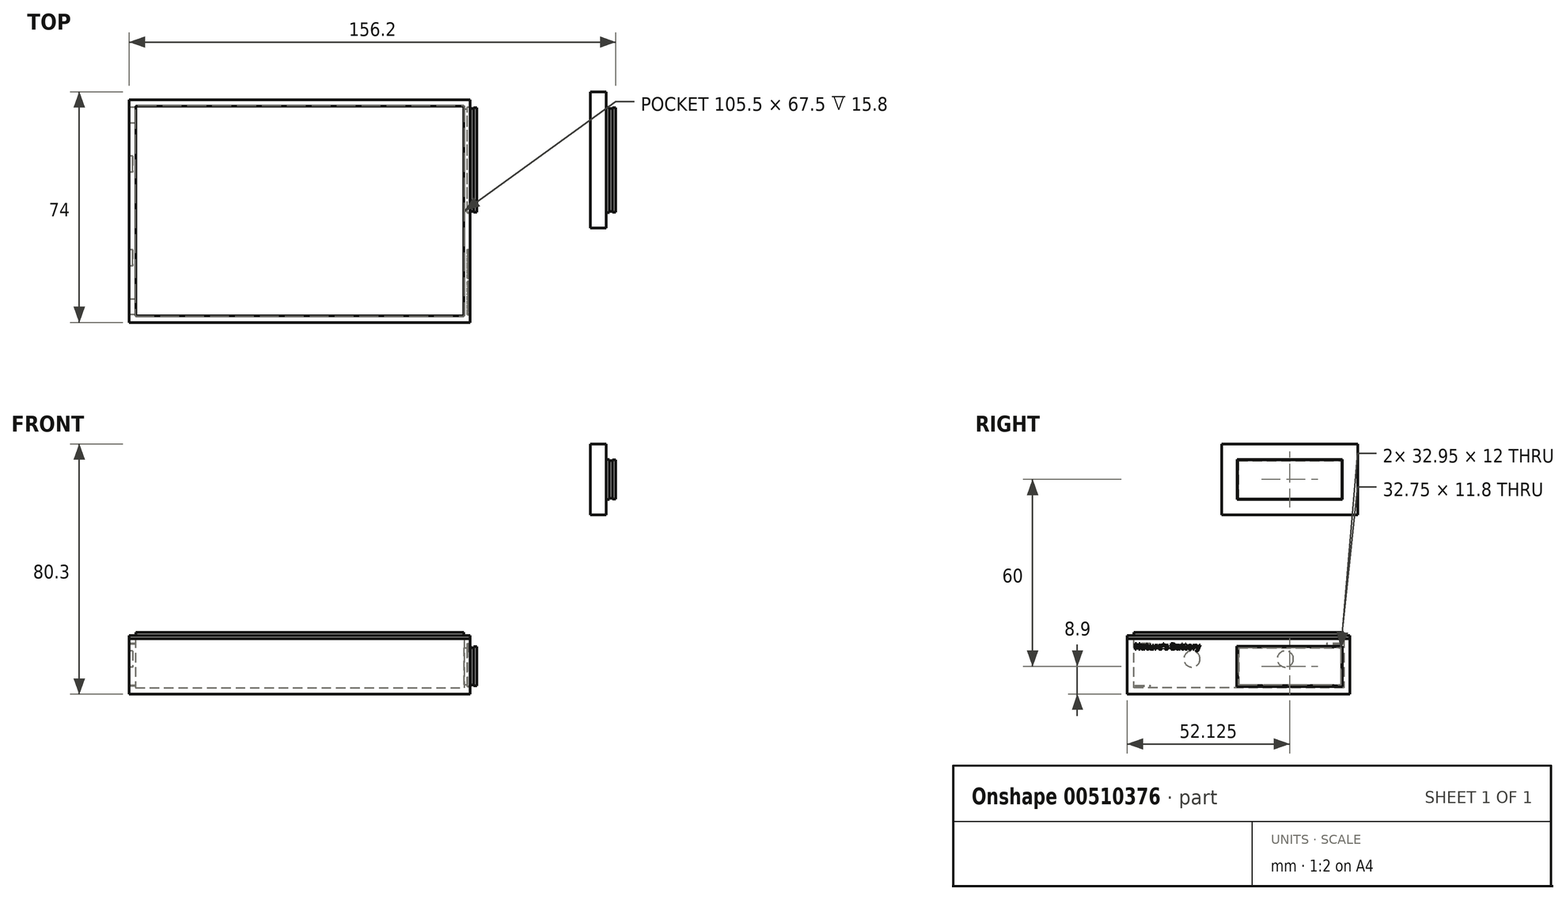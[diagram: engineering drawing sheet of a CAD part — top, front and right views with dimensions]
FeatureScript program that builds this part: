
annotation { "Feature Type Name" : "Feature", "Feature Type Description" : "" }
export const myFeature = defineFeature(function(context is Context, id is Id, definition is map)
    precondition{}
    {
        {
            var Q0;
            Q0=qCreatedBy(makeId("Top.planeOp"),FACE);
            var sketch = newSketch(context, id + "F0", { "sketchPlane" : qUnion([Q0])});
            skLineSegment(sketch, "E0.bottom", {"start": v(-54.75, 35.75) * mm, "end": v(54.75, 35.75) * mm});
            skLineSegment(sketch, "E0.top", {"start": v(-54.75, -35.75) * mm, "end": v(54.75, -35.75) * mm});
            skLineSegment(sketch, "E0.left", {"start": v(-54.75, 35.75) * mm, "end": v(-54.75, -35.75) * mm});
            skLineSegment(sketch, "E0.right", {"start": v(54.75, 35.75) * mm, "end": v(54.75, -35.75) * mm});
            skPoint(sketch, "E0.middle", {"position": v(0, 0) * mm});
            skSolve(sketch);
        }
        {
            var Q0;
            Q0 = qSketchRegion(id + "F0", true);
            extrude(context, id + "F1", {"entities" : qUnion([Q0]), "depth" : 17.8 * mm});
        }
        {
            var Q0;
            Q0=makeQuery(id+"F1.opExtrude","CAP_FACE",FACE,{"disambiguationData":[OSD([sQuery(id+"F0.wireOp",EDGE,"E0.bottom"),sQuery(id+"F0.wireOp",EDGE,"E0.top"),sQuery(id+"F0.wireOp",EDGE,"E0.left"),sQuery(id+"F0.wireOp",EDGE,"E0.right")])],"isStart":false});
            shell(context, id + "F2", {"entities" : qUnion([Q0]), "thickness" : 2 * mm});
        }
        {
            var Q0;
            Q0=makeQuery(id+"F1.opExtrude","CAP_FACE",FACE,{"disambiguationData":[OSD([sQuery(id+"F0.wireOp",EDGE,"E0.bottom"),sQuery(id+"F0.wireOp",EDGE,"E0.top"),sQuery(id+"F0.wireOp",EDGE,"E0.left"),sQuery(id+"F0.wireOp",EDGE,"E0.right")])],"isStart":false});
            var sketch = newSketch(context, id + "F3", { "sketchPlane" : qUnion([Q0])});
            skLineSegment(sketch, "E1.bottom", {"start": v(-54.75, -35.75) * mm, "end": v(54.75, -35.75) * mm});
            skLineSegment(sketch, "E1.top", {"start": v(-54.75, 35.75) * mm, "end": v(54.75, 35.75) * mm});
            skLineSegment(sketch, "E1.left", {"start": v(-54.75, -35.75) * mm, "end": v(-54.75, 35.75) * mm});
            skLineSegment(sketch, "E1.right", {"start": v(54.75, -35.75) * mm, "end": v(54.75, 35.75) * mm});
            skSolve(sketch);
        }
        {
            var Q0;
            Q0 = qSketchRegion(id + "F3", true);
            extrude(context, id + "F4", {"entities" : qUnion([Q0]), "depth" : 1 * mm});
        }
        {
            var Q0;
            Q0=makeQuery(id+"F4.opExtrude","CAP_FACE",FACE,{"disambiguationData":[OSD([sQuery(id+"F3.wireOp",EDGE,"E1.bottom"),sQuery(id+"F3.wireOp",EDGE,"E1.top"),sQuery(id+"F3.wireOp",EDGE,"E1.left"),sQuery(id+"F3.wireOp",EDGE,"E1.right")])],"isStart":false});
            var sketch = newSketch(context, id + "F5", { "sketchPlane" : qUnion([Q0])});
            skPoint(sketch, "E2", {"position": v(52.75, 35.75) * mm});
            skPoint(sketch, "E3", {"position": v(52.65, 33.65) * mm});
            skPoint(sketch, "E4", {"position": v(54.75, 35.75) * mm});
            skPoint(sketch, "E5", {"position": v(54.75, 33.65) * mm});
            skPoint(sketch, "E6", {"position": v(-54.75, -35.75) * mm});
            skPoint(sketch, "E7", {"position": v(-54.75, -33.65) * mm});
            skPoint(sketch, "E8", {"position": v(-52.65, -33.65) * mm});
            skPoint(sketch, "E9", {"position": v(-52.65, -35.75) * mm});
            skLineSegment(sketch, "E10.bottom", {"start": v(-52.65, -33.65) * mm, "end": v(52.65, -33.65) * mm});
            skLineSegment(sketch, "E10.top", {"start": v(-52.65, 33.65) * mm, "end": v(52.65, 33.65) * mm});
            skLineSegment(sketch, "E10.left", {"start": v(-52.65, -33.65) * mm, "end": v(-52.65, 33.65) * mm});
            skLineSegment(sketch, "E10.right", {"start": v(52.65, -33.65) * mm, "end": v(52.65, 33.65) * mm});
            skSolve(sketch);
        }
        {
            var Q0;
            Q0 = qSketchRegion(id + "F5", true);
            extrude(context, id + "F6", {"entities" : qUnion([Q0]), "operationType" : NewBodyOperationType.ADD, "depth" : 1 * mm});
        }
        {
            var Q0;
            Q0=makeQuery(id+"F1.opExtrude","SWEPT_FACE",FACE,{"disambiguationData":[OSD([sQuery(id+"F0.wireOp",EDGE,"E0.left")])]});
            var sketch = newSketch(context, id + "F7", { "sketchPlane" : qUnion([Q0])});
            skPoint(sketch, "E11", {"position": v(33.25, 0) * mm});
            skPoint(sketch, "E12", {"position": v(35.75, 2.5) * mm});
            skPoint(sketch, "E13", {"position": v(35.75, 0) * mm});
            skPoint(sketch, "E14", {"position": v(33.25, 2.5) * mm});
            skLineSegment(sketch, "E15.bottom", {"start": v(33.25, 2.5) * mm, "end": v(28.25, 2.5) * mm});
            skLineSegment(sketch, "E15.top", {"start": v(33.25, 2.8) * mm, "end": v(28.25, 2.8) * mm});
            skLineSegment(sketch, "E15.left", {"start": v(33.25, 2.5) * mm, "end": v(33.25, 2.8) * mm});
            skLineSegment(sketch, "E15.right", {"start": v(28.25, 2.5) * mm, "end": v(28.25, 2.8) * mm});
            skLineSegment(sketch, "E16.bottom", {"start": v(28.25, 16.3) * mm, "end": v(33.25, 16.3) * mm});
            skLineSegment(sketch, "E16.top", {"start": v(28.25, 16) * mm, "end": v(33.25, 16) * mm});
            skLineSegment(sketch, "E16.left", {"start": v(28.25, 16.3) * mm, "end": v(28.25, 16) * mm});
            skLineSegment(sketch, "E16.right", {"start": v(33.25, 16.3) * mm, "end": v(33.25, 16) * mm});
            skPoint(sketch, "E17", {"position": v(-35.75, 0) * mm});
            skPoint(sketch, "E18", {"position": v(-33.25, 0) * mm});
            skPoint(sketch, "E19", {"position": v(-35.75, 2.5) * mm});
            skPoint(sketch, "E20", {"position": v(-33.25, 2.5) * mm});
            skLineSegment(sketch, "E21.bottom", {"start": v(-33.25, 2.5) * mm, "end": v(-28.25, 2.5) * mm});
            skLineSegment(sketch, "E21.top", {"start": v(-33.25, 2.8) * mm, "end": v(-28.25, 2.8) * mm});
            skLineSegment(sketch, "E21.left", {"start": v(-33.25, 2.5) * mm, "end": v(-33.25, 2.8) * mm});
            skLineSegment(sketch, "E21.right", {"start": v(-28.25, 2.5) * mm, "end": v(-28.25, 2.8) * mm});
            skLineSegment(sketch, "E22.bottom", {"start": v(-33.25, 16.3) * mm, "end": v(-28.25, 16.3) * mm});
            skLineSegment(sketch, "E22.top", {"start": v(-33.25, 16) * mm, "end": v(-28.25, 16) * mm});
            skLineSegment(sketch, "E22.left", {"start": v(-33.25, 16.3) * mm, "end": v(-33.25, 16) * mm});
            skLineSegment(sketch, "E22.right", {"start": v(-28.25, 16.3) * mm, "end": v(-28.25, 16) * mm});
            skSolve(sketch);
        }
        {
            var Q0;
            Q0 = qSketchRegion(id + "F7", true);
            extrude(context, id + "F8", {"entities" : qUnion([Q0]), "operationType" : NewBodyOperationType.REMOVE, "oppositeDirection" : true, "depth" : 2 * mm});
        }
        {
            var Q0;
            Q0=makeQuery(id+"F1.opExtrude","SWEPT_FACE",FACE,{"disambiguationData":[OSD([sQuery(id+"F0.wireOp",EDGE,"E0.right")])]});
            var sketch = newSketch(context, id + "F9", { "sketchPlane" : qUnion([Q0])});
            skText(sketch, "E23", { "text": "Nature\'s Battery", "fontName": "OpenSans-Bold.ttf"});
            const initialGuessF9  = {"E23": [-0.0335, 0.01438, 1, 0, 0.00183]};
            skSetInitialGuess(sketch, initialGuessF9);
            skSolve(sketch);
        }
        {
            var Q0;
            Q0 = qSketchRegion(id + "F9", true);
            extrude(context, id + "F10", {"entities" : qUnion([Q0]), "operationType" : NewBodyOperationType.REMOVE, "oppositeDirection" : true, "depth" : 1 * mm});
        }
        {
            var Q0;
            {var subQ0=sQuery(id+"F0.wireOp",EDGE,"E0.bottom");var subQ1=sQuery(id+"F0.wireOp",EDGE,"E0.right");Q0=makeQuery(id+"F10.boolean.opBoolean","SPLIT",FACE,{"disambiguationData":[TD([makeQuery(id+"F1.opExtrude","SWEPT_FACE",FACE,{"disambiguationData":[OSD([subQ0])]})])],"derivedFrom":makeQuery(id+"F1.opExtrude","SWEPT_FACE",FACE,{"disambiguationData":[OSD([subQ1])]})});}
            var sketch = newSketch(context, id + "F11", { "sketchPlane" : qUnion([Q0])});
            skPoint(sketch, "E24", {"position": v(35.75, 0) * mm});
            skPoint(sketch, "E25", {"position": v(32.75, 0) * mm});
            skPoint(sketch, "E26", {"position": v(32.75, 3) * mm});
            skPoint(sketch, "E27", {"position": v(35.75, 3) * mm});
            skPoint(sketch, "E28", {"position": v(32.75, 14.8) * mm});
            skPoint(sketch, "E29", {"position": v(32.75, 17.8) * mm});
            skPoint(sketch, "E30", {"position": v(35.75, 17.8) * mm});
            skPoint(sketch, "E31", {"position": v(35.75, 14.8) * mm});
            skLineSegment(sketch, "E32.bottom", {"start": v(32.75, 3) * mm, "end": v(0, 3) * mm});
            skLineSegment(sketch, "E32.top", {"start": v(32.75, 14.8) * mm, "end": v(0, 14.8) * mm});
            skLineSegment(sketch, "E32.left", {"start": v(32.75, 3) * mm, "end": v(32.75, 14.8) * mm});
            skLineSegment(sketch, "E32.right", {"start": v(0, 3) * mm, "end": v(0, 14.8) * mm});
            skSolve(sketch);
        }
        {
            var Q0;
            Q0 = qSketchRegion(id + "F11", true);
            extrude(context, id + "F12", {"entities" : qUnion([Q0]), "operationType" : NewBodyOperationType.REMOVE, "oppositeDirection" : true, "depth" : 2 * mm});
        }
        {
            var Q0;
            {var subQ0=sQuery(id+"F0.wireOp",EDGE,"E0.bottom");var subQ1=sQuery(id+"F0.wireOp",EDGE,"E0.right");Q0=makeQuery(id+"F10.boolean.opBoolean","SPLIT",FACE,{"disambiguationData":[TD([makeQuery(id+"F1.opExtrude","SWEPT_FACE",FACE,{"disambiguationData":[OSD([subQ0])]})])],"derivedFrom":makeQuery(id+"F1.opExtrude","SWEPT_FACE",FACE,{"disambiguationData":[OSD([subQ1])]})});}
            var sketch = newSketch(context, id + "F13", { "sketchPlane" : qUnion([Q0])});
            skPoint(sketch, "E33", {"position": v(33.35, 15.4) * mm});
            skPoint(sketch, "E34", {"position": v(32.75, 14.8) * mm});
            skPoint(sketch, "E35", {"position": v(32.75, 15.4) * mm});
            skPoint(sketch, "E36", {"position": v(33.35, 14.8) * mm});
            skPoint(sketch, "E37", {"position": v(0, 3) * mm});
            skPoint(sketch, "E38", {"position": v(-0.6, 3) * mm});
            skPoint(sketch, "E39", {"position": v(0, 2.4) * mm});
            skPoint(sketch, "E40", {"position": v(-0.6, 2.4) * mm});
            skLineSegment(sketch, "E41.bottom", {"start": v(-0.6, 2.4) * mm, "end": v(33.35, 2.4) * mm});
            skLineSegment(sketch, "E41.top", {"start": v(-0.6, 15.4) * mm, "end": v(33.35, 15.4) * mm});
            skLineSegment(sketch, "E41.left", {"start": v(-0.6, 2.4) * mm, "end": v(-0.6, 15.4) * mm});
            skLineSegment(sketch, "E41.right", {"start": v(33.35, 2.4) * mm, "end": v(33.35, 15.4) * mm});
            skSolve(sketch);
        }
        {
            var Q0;
            Q0 = qSketchRegion(id + "F13", true);
            extrude(context, id + "F14", {"entities" : qUnion([Q0]), "operationType" : NewBodyOperationType.REMOVE, "oppositeDirection" : true, "depth" : 1 * mm});
        }
        {
            var Q0;
            Q0=makeQuery(id+"F14.boolean.opBoolean","COPY",FACE,{"derivedFrom":makeQuery(id+"F14.opExtrude","CAP_FACE",FACE,{"disambiguationData":[OSD([sQuery(id+"F13.wireOp",EDGE,"E41.bottom"),sQuery(id+"F13.wireOp",EDGE,"E41.top"),sQuery(id+"F13.wireOp",EDGE,"E41.left"),sQuery(id+"F13.wireOp",EDGE,"E41.right")])],"isStart":false})});
            var sketch = newSketch(context, id + "F15", { "sketchPlane" : qUnion([Q0])});
            skPoint(sketch, "E42", {"position": v(33.35, 15.4) * mm});
            skPoint(sketch, "E43", {"position": v(33.35, 15.3) * mm});
            skPoint(sketch, "E44", {"position": v(33.25, 15.4) * mm});
            skPoint(sketch, "E45", {"position": v(33.25, 15.3) * mm});
            skPoint(sketch, "E46", {"position": v(-0.6, 2.4) * mm});
            skPoint(sketch, "E47", {"position": v(-0.5, 2.4) * mm});
            skPoint(sketch, "E48", {"position": v(-0.6, 2.5) * mm});
            skPoint(sketch, "E49", {"position": v(-0.5, 2.5) * mm});
            skLineSegment(sketch, "E50.bottom", {"start": v(-0.5, 2.5) * mm, "end": v(33.25, 2.5) * mm});
            skLineSegment(sketch, "E50.top", {"start": v(-0.5, 15.3) * mm, "end": v(33.25, 15.3) * mm});
            skLineSegment(sketch, "E50.left", {"start": v(-0.5, 2.5) * mm, "end": v(-0.5, 15.3) * mm});
            skLineSegment(sketch, "E50.right", {"start": v(33.25, 2.5) * mm, "end": v(33.25, 15.3) * mm});
            skSolve(sketch);
        }
        {
            var Q0;
            Q0 = qSketchRegion(id + "F15", true);
            extrude(context, id + "F16", {"entities" : qUnion([Q0]), "depth" : 1.1 * mm});
        }
        {
            var Q0;
            Q0=makeQuery(id+"F16.opExtrude","CAP_FACE",FACE,{"disambiguationData":[OSD([sQuery(id+"F15.wireOp",EDGE,"E50.bottom"),sQuery(id+"F15.wireOp",EDGE,"E50.top"),sQuery(id+"F15.wireOp",EDGE,"E50.left"),sQuery(id+"F15.wireOp",EDGE,"E50.right")])],"isStart":false});
            var sketch = newSketch(context, id + "F17", { "sketchPlane" : qUnion([Q0])});
            skPoint(sketch, "E51", {"position": v(-0.5, 15.3) * mm});
            skPoint(sketch, "E52", {"position": v(-0.1, 15.3) * mm});
            skPoint(sketch, "E53", {"position": v(-0.5, 14.9) * mm});
            skPoint(sketch, "E54", {"position": v(-0.1, 14.9) * mm});
            skPoint(sketch, "E55", {"position": v(33.25, 2.5) * mm});
            skPoint(sketch, "E56", {"position": v(32.85, 2.5) * mm});
            skPoint(sketch, "E57", {"position": v(33.25, 2.9) * mm});
            skPoint(sketch, "E58", {"position": v(32.85, 2.9) * mm});
            skLineSegment(sketch, "E59.bottom", {"start": v(-0.1, 14.9) * mm, "end": v(32.85, 14.9) * mm});
            skLineSegment(sketch, "E59.top", {"start": v(-0.1, 2.9) * mm, "end": v(32.85, 2.9) * mm});
            skLineSegment(sketch, "E59.left", {"start": v(-0.1, 14.9) * mm, "end": v(-0.1, 2.9) * mm});
            skLineSegment(sketch, "E59.right", {"start": v(32.85, 14.9) * mm, "end": v(32.85, 2.9) * mm});
            skSolve(sketch);
        }
        {
            var Q0;
            Q0 = qSketchRegion(id + "F17", true);
            extrude(context, id + "F18", {"entities" : qUnion([Q0]), "operationType" : NewBodyOperationType.ADD, "depth" : 2 * mm});
        }
        {
            var Q0;
            Q0=makeQuery(id+"F18.opExtrude","SWEPT_FACE",FACE,{"disambiguationData":[OSD([sQuery(id+"F17.wireOp",EDGE,"E59.left")])]});
            var sketch = newSketch(context, id + "F19", { "sketchPlane" : qUnion([Q0])});
            skLineSegment(sketch, "E60.bottom", {"start": v(56.85, 14.9) * mm, "end": v(55.85, 14.9) * mm});
            skLineSegment(sketch, "E60.top", {"start": v(56.85, 2.9) * mm, "end": v(55.85, 2.9) * mm});
            skLineSegment(sketch, "E60.left", {"start": v(56.85, 14.9) * mm, "end": v(56.85, 2.9) * mm});
            skLineSegment(sketch, "E60.right", {"start": v(55.85, 14.9) * mm, "end": v(55.85, 2.9) * mm});
            skSolve(sketch);
        }
        {
            var Q0;
            Q0 = qSketchRegion(id + "F19", true);
            extrude(context, id + "F20", {"entities" : qUnion([Q0]), "operationType" : NewBodyOperationType.ADD, "depth" : .3 * mm});
        }
        {
            var Q0;
            Q0=makeQuery(id+"F18.opExtrude","SWEPT_FACE",FACE,{"disambiguationData":[OSD([sQuery(id+"F17.wireOp",EDGE,"E59.right")])]});
            var sketch = newSketch(context, id + "F21", { "sketchPlane" : qUnion([Q0])});
            skLineSegment(sketch, "E61.bottom", {"start": v(-56.85, 14.9) * mm, "end": v(-55.85, 14.9) * mm});
            skLineSegment(sketch, "E61.top", {"start": v(-56.85, 2.9) * mm, "end": v(-55.85, 2.9) * mm});
            skLineSegment(sketch, "E61.left", {"start": v(-56.85, 14.9) * mm, "end": v(-56.85, 2.9) * mm});
            skLineSegment(sketch, "E61.right", {"start": v(-55.85, 14.9) * mm, "end": v(-55.85, 2.9) * mm});
            skSolve(sketch);
        }
        {
            var Q0;
            Q0 = qSketchRegion(id + "F21", true);
            extrude(context, id + "F22", {"entities" : qUnion([Q0]), "operationType" : NewBodyOperationType.ADD, "depth" : .3 * mm});
        }
        {
            var Q0;
            Q0=makeQuery(id+"F22.boolean.opBoolean","MERGE",FACE,{"derivedFrom":[makeQuery(id+"F20.boolean.opBoolean","MERGE",FACE,{"derivedFrom":[makeQuery(id+"F18.opExtrude","SWEPT_FACE",FACE,{"disambiguationData":[OSD([sQuery(id+"F17.wireOp",EDGE,"E59.bottom")])]}),makeQuery(id+"F20.opExtrude","SWEPT_FACE",FACE,{"disambiguationData":[OSD([sQuery(id+"F19.wireOp",EDGE,"E60.bottom")])]})]}),makeQuery(id+"F22.opExtrude","SWEPT_FACE",FACE,{"disambiguationData":[OSD([sQuery(id+"F21.wireOp",EDGE,"E61.bottom")])]})]});
            var sketch = newSketch(context, id + "F23", { "sketchPlane" : qUnion([Q0])});
            skLineSegment(sketch, "E62.bottom", {"start": v(55.85, -0.4) * mm, "end": v(56.85, -0.4) * mm});
            skLineSegment(sketch, "E62.top", {"start": v(55.85, 33.15) * mm, "end": v(56.85, 33.15) * mm});
            skLineSegment(sketch, "E62.left", {"start": v(55.85, -0.4) * mm, "end": v(55.85, 33.15) * mm});
            skLineSegment(sketch, "E62.right", {"start": v(56.85, -0.4) * mm, "end": v(56.85, 33.15) * mm});
            skSolve(sketch);
        }
        {
            var Q0;
            Q0 = qSketchRegion(id + "F23", true);
            extrude(context, id + "F24", {"entities" : qUnion([Q0]), "operationType" : NewBodyOperationType.ADD, "depth" : .3 * mm});
        }
        {
            var Q0;
            Q0=makeQuery(id+"F22.boolean.opBoolean","MERGE",FACE,{"derivedFrom":[makeQuery(id+"F20.boolean.opBoolean","MERGE",FACE,{"derivedFrom":[makeQuery(id+"F18.opExtrude","SWEPT_FACE",FACE,{"disambiguationData":[OSD([sQuery(id+"F17.wireOp",EDGE,"E59.top")])]}),makeQuery(id+"F20.opExtrude","SWEPT_FACE",FACE,{"disambiguationData":[OSD([sQuery(id+"F19.wireOp",EDGE,"E60.top")])]})]}),makeQuery(id+"F22.opExtrude","SWEPT_FACE",FACE,{"disambiguationData":[OSD([sQuery(id+"F21.wireOp",EDGE,"E61.top")])]})]});
            var sketch = newSketch(context, id + "F25", { "sketchPlane" : qUnion([Q0])});
            skLineSegment(sketch, "E63.bottom", {"start": v(55.85, 0.4) * mm, "end": v(56.85, 0.4) * mm});
            skLineSegment(sketch, "E63.top", {"start": v(55.85, -33.15) * mm, "end": v(56.85, -33.15) * mm});
            skLineSegment(sketch, "E63.left", {"start": v(55.85, 0.4) * mm, "end": v(55.85, -33.15) * mm});
            skLineSegment(sketch, "E63.right", {"start": v(56.85, 0.4) * mm, "end": v(56.85, -33.15) * mm});
            skSolve(sketch);
        }
        {
            var Q0;
            Q0 = qSketchRegion(id + "F25", true);
            extrude(context, id + "F26", {"entities" : qUnion([Q0]), "operationType" : NewBodyOperationType.ADD, "depth" : .3 * mm});
        }
        {
            var Q0;
            Q0=makeQuery(id+"F1.opExtrude","SWEPT_FACE",FACE,{"disambiguationData":[OSD([sQuery(id+"F0.wireOp",EDGE,"E0.left")])]});
            var sketch = newSketch(context, id + "F27", { "sketchPlane" : qUnion([Q0])});
            skPoint(sketch, "E64", {"position": v(0, 11.24) * mm});
            skPoint(sketch, "E64.positionSnap0", {"position": v(0, 17.8) * mm});
            skCircle(sketch, "E65", {"center": v(-15, 11.24) * mm, "radius": 2.6 * mm});
            skCircle(sketch, "E66", {"center": v(15, 11.25) * mm, "radius": 2.6 * mm});
            skSolve(sketch);
        }
        {
            var Q0;
            Q0 = qSketchRegion(id + "F27", true);
            extrude(context, id + "F28", {"entities" : qUnion([Q0]), "operationType" : NewBodyOperationType.REMOVE, "oppositeDirection" : true, "depth" : 1.1 * mm});
        }
        {
            var Q0;
            Q0=makeQuery(id+"F16.opExtrude","SWEPT_BODY",BODY,{"disambiguationData":[OSD([sQuery(id+"F15.wireOp",EDGE,"E50.bottom"),sQuery(id+"F15.wireOp",EDGE,"E50.top"),sQuery(id+"F15.wireOp",EDGE,"E50.left"),sQuery(id+"F15.wireOp",EDGE,"E50.right")])]});
            transform(context, id + "F29", {"entities" : qUnion([Q0]), "transformType" : TransformType.TRANSLATION_3D, "dx" : 0 * mm, "dy" : 0 * mm, "dz" : 0 * mm, "makeCopy" : true});
        }
        {
            var Q0;
            Q0=makeQuery(id+"F29.opPattern","COPY",BODY,{"derivedFrom":makeQuery(id+"F16.opExtrude","SWEPT_BODY",BODY,{"disambiguationData":[OSD([sQuery(id+"F15.wireOp",EDGE,"E50.bottom"),sQuery(id+"F15.wireOp",EDGE,"E50.top"),sQuery(id+"F15.wireOp",EDGE,"E50.left"),sQuery(id+"F15.wireOp",EDGE,"E50.right")])]}),"instanceName":"1"});
            deleteBodies(context, id + "F30", {"entities" : qUnion([Q0])});
        }
        {
            var Q0;
            Q0=makeQuery(id+"F16.opExtrude","SWEPT_BODY",BODY,{"disambiguationData":[OSD([sQuery(id+"F15.wireOp",EDGE,"E50.bottom"),sQuery(id+"F15.wireOp",EDGE,"E50.top"),sQuery(id+"F15.wireOp",EDGE,"E50.left"),sQuery(id+"F15.wireOp",EDGE,"E50.right")])]});
            transform(context, id + "F31", {"entities" : qUnion([Q0]), "transformType" : TransformType.TRANSLATION_3D, "dx" : 76 * mm, "dy" : 0 * mm, "dz" : 0 * mm, "makeCopy" : true});
        }
        {
            var Q0;
            Q0=makeQuery(id+"F31.opPattern","COPY",FACE,{"derivedFrom":makeQuery(id+"F24.opExtrude","CAP_FACE",FACE,{"disambiguationData":[OSD([sQuery(id+"F23.wireOp",EDGE,"E62.bottom"),sQuery(id+"F23.wireOp",EDGE,"E62.top"),sQuery(id+"F23.wireOp",EDGE,"E62.left"),sQuery(id+"F23.wireOp",EDGE,"E62.right")])],"isStart":false}),"instanceName":"1"});
            var sketch = newSketch(context, id + "F32", { "sketchPlane" : qUnion([Q0])});
            skLineSegment(sketch, "E67.bottom", {"start": v(131.85, 33.15) * mm, "end": v(132.85, 33.15) * mm});
            skLineSegment(sketch, "E67.top", {"start": v(131.85, -0.4) * mm, "end": v(132.85, -0.4) * mm});
            skLineSegment(sketch, "E67.left", {"start": v(131.85, 33.15) * mm, "end": v(131.85, -0.4) * mm});
            skLineSegment(sketch, "E67.right", {"start": v(132.85, 33.15) * mm, "end": v(132.85, -0.4) * mm});
            skSolve(sketch);
        }
        {
            var Q0;
            Q0 = qSketchRegion(id + "F32", true);
            extrude(context, id + "F33", {"entities" : qUnion([Q0]), "depth" : 5 * mm, "offsetDistance" : 25 * mm});
        }
        {
            var Q0;
            Q0=makeQuery(id+"F31.opPattern","COPY",FACE,{"derivedFrom":makeQuery(id+"F22.boolean.opBoolean","MERGE",FACE,{"derivedFrom":[makeQuery(id+"F20.boolean.opBoolean","MERGE",FACE,{"derivedFrom":[makeQuery(id+"F18.opExtrude","SWEPT_FACE",FACE,{"disambiguationData":[OSD([sQuery(id+"F17.wireOp",EDGE,"E59.bottom")])]}),makeQuery(id+"F20.opExtrude","SWEPT_FACE",FACE,{"disambiguationData":[OSD([sQuery(id+"F19.wireOp",EDGE,"E60.bottom")])]})]}),makeQuery(id+"F22.opExtrude","SWEPT_FACE",FACE,{"disambiguationData":[OSD([sQuery(id+"F21.wireOp",EDGE,"E61.bottom")])]})]}),"instanceName":"1"});
            var sketch = newSketch(context, id + "F34", { "sketchPlane" : qUnion([Q0])});
            skLineSegment(sketch, "E68.bottom", {"start": v(131.85, 32.85) * mm, "end": v(130.85, 32.85) * mm});
            skLineSegment(sketch, "E68.top", {"start": v(131.85, -0.1) * mm, "end": v(130.85, -0.1) * mm});
            skLineSegment(sketch, "E68.left", {"start": v(131.85, 32.85) * mm, "end": v(131.85, -0.1) * mm});
            skLineSegment(sketch, "E68.right", {"start": v(130.85, 32.85) * mm, "end": v(130.85, -0.1) * mm});
            skSolve(sketch);
        }
        {
            var Q0;
            Q0 = qSketchRegion(id + "F34", true);
            extrude(context, id + "F35", {"entities" : qUnion([Q0]), "depth" : 5.3 * mm, "offsetDistance" : 25 * mm});
        }
        {
            var Q0;
            Q0=makeQuery(id+"F31.opPattern","COPY",FACE,{"derivedFrom":makeQuery(id+"F16.opExtrude","SWEPT_FACE",FACE,{"disambiguationData":[OSD([sQuery(id+"F15.wireOp",EDGE,"E50.top")])]}),"instanceName":"1"});
            var sketch = newSketch(context, id + "F36", { "sketchPlane" : qUnion([Q0])});
            skLineSegment(sketch, "E69.bottom", {"start": v(130.85, 33.25) * mm, "end": v(129.75, 33.25) * mm});
            skLineSegment(sketch, "E69.top", {"start": v(130.85, -0.5) * mm, "end": v(129.75, -0.5) * mm});
            skLineSegment(sketch, "E69.left", {"start": v(130.85, 33.25) * mm, "end": v(130.85, -0.5) * mm});
            skLineSegment(sketch, "E69.right", {"start": v(129.75, 33.25) * mm, "end": v(129.75, -0.5) * mm});
            skSolve(sketch);
        }
        {
            var Q0;
            Q0 = qSketchRegion(id + "F36", true);
            extrude(context, id + "F37", {"entities" : qUnion([Q0]), "depth" : 4.9 * mm, "offsetDistance" : 25 * mm});
        }
        {
            var Q0;
            Q0=makeQuery(id+"F31.opPattern","COPY",FACE,{"derivedFrom":makeQuery(id+"F22.boolean.opBoolean","MERGE",FACE,{"derivedFrom":[makeQuery(id+"F20.boolean.opBoolean","MERGE",FACE,{"derivedFrom":[makeQuery(id+"F18.opExtrude","SWEPT_FACE",FACE,{"disambiguationData":[OSD([sQuery(id+"F17.wireOp",EDGE,"E59.top")])]}),makeQuery(id+"F20.opExtrude","SWEPT_FACE",FACE,{"disambiguationData":[OSD([sQuery(id+"F19.wireOp",EDGE,"E60.top")])]})]}),makeQuery(id+"F22.opExtrude","SWEPT_FACE",FACE,{"disambiguationData":[OSD([sQuery(id+"F21.wireOp",EDGE,"E61.top")])]})]}),"instanceName":"1"});
            var sketch = newSketch(context, id + "F38", { "sketchPlane" : qUnion([Q0])});
            skLineSegment(sketch, "E70.bottom", {"start": v(130.85, 0.1) * mm, "end": v(131.85, 0.1) * mm});
            skLineSegment(sketch, "E70.top", {"start": v(130.85, -32.85) * mm, "end": v(131.85, -32.85) * mm});
            skLineSegment(sketch, "E70.left", {"start": v(130.85, 0.1) * mm, "end": v(130.85, -32.85) * mm});
            skLineSegment(sketch, "E70.right", {"start": v(131.85, 0.1) * mm, "end": v(131.85, -32.85) * mm});
            skSolve(sketch);
        }
        {
            var Q0;
            Q0 = qSketchRegion(id + "F38", true);
            extrude(context, id + "F39", {"entities" : qUnion([Q0]), "depth" : 5.4 * mm, "offsetDistance" : 25 * mm});
        }
        {
            var Q0;
            Q0=makeQuery(id+"F31.opPattern","COPY",FACE,{"derivedFrom":makeQuery(id+"F26.opExtrude","CAP_FACE",FACE,{"disambiguationData":[OSD([sQuery(id+"F25.wireOp",EDGE,"E63.bottom"),sQuery(id+"F25.wireOp",EDGE,"E63.top"),sQuery(id+"F25.wireOp",EDGE,"E63.left"),sQuery(id+"F25.wireOp",EDGE,"E63.right")])],"isStart":false}),"instanceName":"1"});
            var sketch = newSketch(context, id + "F40", { "sketchPlane" : qUnion([Q0])});
            skLineSegment(sketch, "E71.bottom", {"start": v(131.85, -33.15) * mm, "end": v(132.85, -33.15) * mm});
            skLineSegment(sketch, "E71.top", {"start": v(131.85, 0.4) * mm, "end": v(132.85, 0.4) * mm});
            skLineSegment(sketch, "E71.left", {"start": v(131.85, -33.15) * mm, "end": v(131.85, 0.4) * mm});
            skLineSegment(sketch, "E71.right", {"start": v(132.85, -33.15) * mm, "end": v(132.85, 0.4) * mm});
            skSolve(sketch);
        }
        {
            var Q0;
            Q0 = qSketchRegion(id + "F40", true);
            extrude(context, id + "F41", {"entities" : qUnion([Q0]), "depth" : 5.1 * mm, "offsetDistance" : 25 * mm});
        }
        {
            var Q0;
            Q0=makeQuery(id+"F31.opPattern","COPY",FACE,{"derivedFrom":makeQuery(id+"F16.opExtrude","SWEPT_FACE",FACE,{"disambiguationData":[OSD([sQuery(id+"F15.wireOp",EDGE,"E50.bottom")])]}),"instanceName":"1"});
            var sketch = newSketch(context, id + "F42", { "sketchPlane" : qUnion([Q0])});
            skLineSegment(sketch, "E72.bottom", {"start": v(130.85, 0.5) * mm, "end": v(129.75, 0.5) * mm});
            skLineSegment(sketch, "E72.top", {"start": v(130.85, -33.25) * mm, "end": v(129.75, -33.25) * mm});
            skLineSegment(sketch, "E72.left", {"start": v(130.85, 0.5) * mm, "end": v(130.85, -33.25) * mm});
            skLineSegment(sketch, "E72.right", {"start": v(129.75, 0.5) * mm, "end": v(129.75, -33.25) * mm});
            skSolve(sketch);
        }
        {
            var Q0;
            Q0 = qSketchRegion(id + "F42", true);
            extrude(context, id + "F43", {"entities" : qUnion([Q0]), "depth" : 5 * mm, "offsetDistance" : 25 * mm});
        }
        {
            var Q0;
            Q0=makeQuery(id+"F39.opExtrude","SWEPT_FACE",FACE,{"disambiguationData":[OSD([sQuery(id+"F38.wireOp",EDGE,"E70.bottom")])]});
            var sketch = newSketch(context, id + "F44", { "sketchPlane" : qUnion([Q0])});
            skLineSegment(sketch, "E73.bottom", {"start": v(131.85, -2.5) * mm, "end": v(130.85, -2.5) * mm});
            skLineSegment(sketch, "E73.top", {"start": v(131.85, 2.9) * mm, "end": v(130.85, 2.9) * mm});
            skLineSegment(sketch, "E73.left", {"start": v(131.85, -2.5) * mm, "end": v(131.85, 2.9) * mm});
            skLineSegment(sketch, "E73.right", {"start": v(130.85, -2.5) * mm, "end": v(130.85, 2.9) * mm});
            skSolve(sketch);
        }
        {
            var Q0;
            Q0 = qSketchRegion(id + "F44", true);
            extrude(context, id + "F45", {"entities" : qUnion([Q0]), "depth" : 5.1 * mm, "offsetDistance" : 25 * mm});
        }
        {
            var Q0;
            Q0=makeQuery(id+"F43.opExtrude","SWEPT_FACE",FACE,{"disambiguationData":[OSD([sQuery(id+"F42.wireOp",EDGE,"E72.bottom")])]});
            var sketch = newSketch(context, id + "F46", { "sketchPlane" : qUnion([Q0])});
            skLineSegment(sketch, "E74.bottom", {"start": v(130.85, -2.5) * mm, "end": v(129.75, -2.5) * mm});
            skLineSegment(sketch, "E74.top", {"start": v(130.85, 2.5) * mm, "end": v(129.75, 2.5) * mm});
            skLineSegment(sketch, "E74.left", {"start": v(130.85, -2.5) * mm, "end": v(130.85, 2.5) * mm});
            skLineSegment(sketch, "E74.right", {"start": v(129.75, -2.5) * mm, "end": v(129.75, 2.5) * mm});
            skSolve(sketch);
        }
        {
            var Q0;
            Q0 = qSketchRegion(id + "F46", true);
            extrude(context, id + "F47", {"entities" : qUnion([Q0]), "depth" : 4.9 * mm, "offsetDistance" : 25 * mm});
        }
        {
            var Q0;
            Q0=makeQuery(id+"F41.opExtrude","SWEPT_FACE",FACE,{"disambiguationData":[OSD([sQuery(id+"F40.wireOp",EDGE,"E71.top")])]});
            var sketch = newSketch(context, id + "F48", { "sketchPlane" : qUnion([Q0])});
            skLineSegment(sketch, "E75.bottom", {"start": v(132.85, -2.5) * mm, "end": v(131.85, -2.5) * mm});
            skLineSegment(sketch, "E75.top", {"start": v(132.85, 2.6) * mm, "end": v(131.85, 2.6) * mm});
            skLineSegment(sketch, "E75.left", {"start": v(132.85, -2.5) * mm, "end": v(132.85, 2.6) * mm});
            skLineSegment(sketch, "E75.right", {"start": v(131.85, -2.5) * mm, "end": v(131.85, 2.6) * mm});
            skSolve(sketch);
        }
        {
            var Q0;
            Q0 = qSketchRegion(id + "F48", true);
            extrude(context, id + "F49", {"entities" : qUnion([Q0]), "depth" : 4.9 * mm, "offsetDistance" : 25 * mm});
        }
        {
            var Q0;
            Q0=makeQuery(id+"F31.opPattern","COPY",FACE,{"derivedFrom":makeQuery(id+"F26.boolean.opBoolean","MERGE",FACE,{"derivedFrom":[makeQuery(id+"F24.boolean.opBoolean","MERGE",FACE,{"derivedFrom":[makeQuery(id+"F20.opExtrude","CAP_FACE",FACE,{"disambiguationData":[OSD([sQuery(id+"F19.wireOp",EDGE,"E60.bottom"),sQuery(id+"F19.wireOp",EDGE,"E60.top"),sQuery(id+"F19.wireOp",EDGE,"E60.left"),sQuery(id+"F19.wireOp",EDGE,"E60.right")])],"isStart":false}),makeQuery(id+"F24.opExtrude","SWEPT_FACE",FACE,{"disambiguationData":[OSD([sQuery(id+"F23.wireOp",EDGE,"E62.bottom")])]})]}),makeQuery(id+"F26.opExtrude","SWEPT_FACE",FACE,{"disambiguationData":[OSD([sQuery(id+"F25.wireOp",EDGE,"E63.bottom")])]})]}),"instanceName":"1"});
            var sketch = newSketch(context, id + "F50", { "sketchPlane" : qUnion([Q0])});
            skLineSegment(sketch, "E76.bottom", {"start": v(132.85, 2.6) * mm, "end": v(131.85, 2.6) * mm});
            skLineSegment(sketch, "E76.top", {"start": v(132.85, 15.2) * mm, "end": v(131.85, 15.2) * mm});
            skLineSegment(sketch, "E76.left", {"start": v(132.85, 2.6) * mm, "end": v(132.85, 15.2) * mm});
            skLineSegment(sketch, "E76.right", {"start": v(131.85, 2.6) * mm, "end": v(131.85, 15.2) * mm});
            skSolve(sketch);
        }
        {
            var Q0;
            Q0 = qSketchRegion(id + "F50", true);
            extrude(context, id + "F51", {"entities" : qUnion([Q0]), "depth" : 4.9 * mm, "offsetDistance" : 25 * mm});
        }
        {
            var Q0;
            Q0=makeQuery(id+"F31.opPattern","COPY",FACE,{"derivedFrom":makeQuery(id+"F18.opExtrude","SWEPT_FACE",FACE,{"disambiguationData":[OSD([sQuery(id+"F17.wireOp",EDGE,"E59.left")])]}),"instanceName":"1"});
            var sketch = newSketch(context, id + "F52", { "sketchPlane" : qUnion([Q0])});
            skLineSegment(sketch, "E77.bottom", {"start": v(131.85, 2.9) * mm, "end": v(130.85, 2.9) * mm});
            skLineSegment(sketch, "E77.top", {"start": v(131.85, 14.9) * mm, "end": v(130.85, 14.9) * mm});
            skLineSegment(sketch, "E77.left", {"start": v(131.85, 2.9) * mm, "end": v(131.85, 14.9) * mm});
            skLineSegment(sketch, "E77.right", {"start": v(130.85, 2.9) * mm, "end": v(130.85, 14.9) * mm});
            skSolve(sketch);
        }
        {
            var Q0;
            Q0 = qSketchRegion(id + "F52", true);
            extrude(context, id + "F53", {"entities" : qUnion([Q0]), "depth" : 5 * mm, "offsetDistance" : 25 * mm});
        }
        {
            var Q0;
            Q0=makeQuery(id+"F31.opPattern","COPY",FACE,{"derivedFrom":makeQuery(id+"F16.opExtrude","SWEPT_FACE",FACE,{"disambiguationData":[OSD([sQuery(id+"F15.wireOp",EDGE,"E50.left")])]}),"instanceName":"1"});
            var sketch = newSketch(context, id + "F54", { "sketchPlane" : qUnion([Q0])});
            skLineSegment(sketch, "E78.bottom", {"start": v(130.85, 2.5) * mm, "end": v(129.75, 2.5) * mm});
            skLineSegment(sketch, "E78.top", {"start": v(130.85, 15.3) * mm, "end": v(129.75, 15.3) * mm});
            skLineSegment(sketch, "E78.left", {"start": v(130.85, 2.5) * mm, "end": v(130.85, 15.3) * mm});
            skLineSegment(sketch, "E78.right", {"start": v(129.75, 2.5) * mm, "end": v(129.75, 15.3) * mm});
            skSolve(sketch);
        }
        {
            var Q0;
            Q0 = qSketchRegion(id + "F54", true);
            extrude(context, id + "F55", {"entities" : qUnion([Q0]), "depth" : 5 * mm, "offsetDistance" : 25 * mm});
        }
        {
            var Q0;
            Q0=makeQuery(id+"F33.opExtrude","SWEPT_FACE",FACE,{"disambiguationData":[OSD([sQuery(id+"F32.wireOp",EDGE,"E67.top")])]});
            var sketch = newSketch(context, id + "F56", { "sketchPlane" : qUnion([Q0])});
            skLineSegment(sketch, "E79.bottom", {"start": v(132.85, 15.2) * mm, "end": v(131.85, 15.2) * mm});
            skLineSegment(sketch, "E79.top", {"start": v(132.85, 20.2) * mm, "end": v(131.85, 20.2) * mm});
            skLineSegment(sketch, "E79.left", {"start": v(132.85, 15.2) * mm, "end": v(132.85, 20.2) * mm});
            skLineSegment(sketch, "E79.right", {"start": v(131.85, 15.2) * mm, "end": v(131.85, 20.2) * mm});
            skSolve(sketch);
        }
        {
            var Q0;
            Q0 = qSketchRegion(id + "F56", true);
            extrude(context, id + "F57", {"entities" : qUnion([Q0]), "depth" : 5 * mm, "offsetDistance" : 25 * mm});
        }
        {
            var Q0;
            Q0=makeQuery(id+"F35.opExtrude","SWEPT_FACE",FACE,{"disambiguationData":[OSD([sQuery(id+"F34.wireOp",EDGE,"E68.top")])]});
            var sketch = newSketch(context, id + "F58", { "sketchPlane" : qUnion([Q0])});
            skLineSegment(sketch, "E80.bottom", {"start": v(131.85, 14.9) * mm, "end": v(130.85, 14.9) * mm});
            skLineSegment(sketch, "E80.top", {"start": v(131.85, 20.2) * mm, "end": v(130.85, 20.2) * mm});
            skLineSegment(sketch, "E80.left", {"start": v(131.85, 14.9) * mm, "end": v(131.85, 20.2) * mm});
            skLineSegment(sketch, "E80.right", {"start": v(130.85, 14.9) * mm, "end": v(130.85, 20.2) * mm});
            skSolve(sketch);
        }
        {
            var Q0;
            Q0 = qSketchRegion(id + "F58", true);
            extrude(context, id + "F59", {"entities" : qUnion([Q0]), "depth" : 5 * mm, "offsetDistance" : 25 * mm});
        }
        {
            var Q0;
            Q0=makeQuery(id+"F37.opExtrude","SWEPT_FACE",FACE,{"disambiguationData":[OSD([sQuery(id+"F36.wireOp",EDGE,"E69.top")])]});
            var sketch = newSketch(context, id + "F60", { "sketchPlane" : qUnion([Q0])});
            skLineSegment(sketch, "E81.bottom", {"start": v(130.85, 15.3) * mm, "end": v(129.75, 15.3) * mm});
            skLineSegment(sketch, "E81.top", {"start": v(130.85, 20.2) * mm, "end": v(129.75, 20.2) * mm});
            skLineSegment(sketch, "E81.left", {"start": v(130.85, 15.3) * mm, "end": v(130.85, 20.2) * mm});
            skLineSegment(sketch, "E81.right", {"start": v(129.75, 15.3) * mm, "end": v(129.75, 20.2) * mm});
            skSolve(sketch);
        }
        {
            var Q0;
            Q0 = qSketchRegion(id + "F60", true);
            extrude(context, id + "F61", {"entities" : qUnion([Q0]), "depth" : 5 * mm, "offsetDistance" : 25 * mm});
        }
        {
            var Q0;
            Q0=makeQuery(id+"F33.opExtrude","SWEPT_FACE",FACE,{"disambiguationData":[OSD([sQuery(id+"F32.wireOp",EDGE,"E67.bottom")])]});
            var sketch = newSketch(context, id + "F62", { "sketchPlane" : qUnion([Q0])});
            skLineSegment(sketch, "E82.bottom", {"start": v(-132.85, 20.2) * mm, "end": v(-131.85, 20.2) * mm});
            skLineSegment(sketch, "E82.top", {"start": v(-132.85, 15.2) * mm, "end": v(-131.85, 15.2) * mm});
            skLineSegment(sketch, "E82.left", {"start": v(-132.85, 20.2) * mm, "end": v(-132.85, 15.2) * mm});
            skLineSegment(sketch, "E82.right", {"start": v(-131.85, 20.2) * mm, "end": v(-131.85, 15.2) * mm});
            skLineSegment(sketch, "E83.top", {"start": v(-132.85, -2.52) * mm, "end": v(-131.85, -2.52) * mm});
            skLineSegment(sketch, "E83.left", {"start": v(-132.85, 15.2) * mm, "end": v(-132.85, -2.52) * mm});
            skLineSegment(sketch, "E83.right", {"start": v(-131.85, 15.2) * mm, "end": v(-131.85, -2.52) * mm});
            skSolve(sketch);
        }
        {
            var Q0;
            Q0 = qSketchRegion(id + "F62", true);
            extrude(context, id + "F63", {"entities" : qUnion([Q0]), "depth" : 5 * mm, "offsetDistance" : 25 * mm});
        }
        {
            var Q0;
            Q0=makeQuery(id+"F35.opExtrude","SWEPT_FACE",FACE,{"disambiguationData":[OSD([sQuery(id+"F34.wireOp",EDGE,"E68.bottom")])]});
            var sketch = newSketch(context, id + "F64", { "sketchPlane" : qUnion([Q0])});
            skLineSegment(sketch, "E84.bottom", {"start": v(-131.85, 20.2) * mm, "end": v(-130.85, 20.2) * mm});
            skLineSegment(sketch, "E84.top", {"start": v(-131.85, -2.49) * mm, "end": v(-130.85, -2.49) * mm});
            skLineSegment(sketch, "E84.left", {"start": v(-131.85, 20.2) * mm, "end": v(-131.85, -2.49) * mm});
            skLineSegment(sketch, "E84.right", {"start": v(-130.85, 20.2) * mm, "end": v(-130.85, -2.49) * mm});
            skSolve(sketch);
        }
        {
            var Q0;
            Q0 = qSketchRegion(id + "F64", true);
            extrude(context, id + "F65", {"entities" : qUnion([Q0]), "depth" : 5 * mm, "offsetDistance" : 25 * mm});
        }
        {
            var Q0;
            Q0=makeQuery(id+"F37.opExtrude","SWEPT_FACE",FACE,{"disambiguationData":[OSD([sQuery(id+"F36.wireOp",EDGE,"E69.bottom")])]});
            var sketch = newSketch(context, id + "F66", { "sketchPlane" : qUnion([Q0])});
            skLineSegment(sketch, "E85.bottom", {"start": v(-130.85, 20.2) * mm, "end": v(-129.75, 20.2) * mm});
            skLineSegment(sketch, "E85.top", {"start": v(-130.85, -2.5) * mm, "end": v(-129.75, -2.5) * mm});
            skLineSegment(sketch, "E85.left", {"start": v(-130.85, 20.2) * mm, "end": v(-130.85, -2.5) * mm});
            skLineSegment(sketch, "E85.right", {"start": v(-129.75, 20.2) * mm, "end": v(-129.75, -2.5) * mm});
            skSolve(sketch);
        }
        {
            var Q0;
            Q0 = qSketchRegion(id + "F66", true);
            extrude(context, id + "F67", {"entities" : qUnion([Q0]), "depth" : 5 * mm, "offsetDistance" : 25 * mm});
        }
        {
            var Q0;
            Q0=makeQuery(id+"F67.opExtrude","SWEPT_FACE",FACE,{"disambiguationData":[OSD([sQuery(id+"F66.wireOp",EDGE,"E85.right")])]});
            var sketch = newSketch(context, id + "F68", { "sketchPlane" : qUnion([Q0])});
            skLineSegment(sketch, "E86.bottom", {"start": v(-38.25, 20.2) * mm, "end": v(5.4, 20.2) * mm});
            skLineSegment(sketch, "E86.top", {"start": v(-38.25, -2.5) * mm, "end": v(5.4, -2.5) * mm});
            skLineSegment(sketch, "E86.left", {"start": v(-38.25, 20.2) * mm, "end": v(-38.25, -2.5) * mm});
            skLineSegment(sketch, "E86.right", {"start": v(5.4, 20.2) * mm, "end": v(5.4, -2.5) * mm});
            skSolve(sketch);
        }
        {
            var Q0;
            Q0 = qSketchRegion(id + "F68", true);
            extrude(context, id + "F69", {"entities" : qUnion([Q0]), "depth" : 5 * mm, "offsetDistance" : 25 * mm});
        }
        {
            var Q0;
            Q0=makeQuery(id+"F35.opExtrude","SWEPT_BODY",BODY,{"disambiguationData":[OSD([sQuery(id+"F34.wireOp",EDGE,"E68.bottom"),sQuery(id+"F34.wireOp",EDGE,"E68.top"),sQuery(id+"F34.wireOp",EDGE,"E68.left"),sQuery(id+"F34.wireOp",EDGE,"E68.right")])]});
            var Q1;
            Q1=makeQuery(id+"F33.opExtrude","SWEPT_BODY",BODY,{"disambiguationData":[OSD([sQuery(id+"F32.wireOp",EDGE,"E67.bottom"),sQuery(id+"F32.wireOp",EDGE,"E67.top"),sQuery(id+"F32.wireOp",EDGE,"E67.left"),sQuery(id+"F32.wireOp",EDGE,"E67.right")])]});
            var Q2;
            Q2=makeQuery(id+"F37.opExtrude","SWEPT_BODY",BODY,{"disambiguationData":[OSD([sQuery(id+"F36.wireOp",EDGE,"E69.bottom"),sQuery(id+"F36.wireOp",EDGE,"E69.top"),sQuery(id+"F36.wireOp",EDGE,"E69.left"),sQuery(id+"F36.wireOp",EDGE,"E69.right")])]});
            var Q3;
            Q3=makeQuery(id+"F67.opExtrude","SWEPT_BODY",BODY,{"disambiguationData":[OSD([sQuery(id+"F66.wireOp",EDGE,"E85.bottom"),sQuery(id+"F66.wireOp",EDGE,"E85.top"),sQuery(id+"F66.wireOp",EDGE,"E85.left"),sQuery(id+"F66.wireOp",EDGE,"E85.right")])]});
            var Q4;
            Q4=makeQuery(id+"F39.opExtrude","SWEPT_BODY",BODY,{"disambiguationData":[OSD([sQuery(id+"F38.wireOp",EDGE,"E70.bottom"),sQuery(id+"F38.wireOp",EDGE,"E70.top"),sQuery(id+"F38.wireOp",EDGE,"E70.left"),sQuery(id+"F38.wireOp",EDGE,"E70.right")])]});
            deleteBodies(context, id + "F70", {"entities" : qUnion([Q0, Q1, Q2, Q3, Q4])});
        }
        {
            var Q0;
            Q0=makeQuery(id+"F43.opExtrude","SWEPT_BODY",BODY,{"disambiguationData":[OSD([sQuery(id+"F42.wireOp",EDGE,"E72.bottom"),sQuery(id+"F42.wireOp",EDGE,"E72.top"),sQuery(id+"F42.wireOp",EDGE,"E72.left"),sQuery(id+"F42.wireOp",EDGE,"E72.right")])]});
            deleteBodies(context, id + "F71", {"entities" : qUnion([Q0])});
        }
        {
            var Q0;
            Q0=makeQuery(id+"F49.opExtrude","SWEPT_BODY",BODY,{"disambiguationData":[OSD([sQuery(id+"F48.wireOp",EDGE,"E75.bottom"),sQuery(id+"F48.wireOp",EDGE,"E75.top"),sQuery(id+"F48.wireOp",EDGE,"E75.left"),sQuery(id+"F48.wireOp",EDGE,"E75.right")])]});
            var Q1;
            Q1=makeQuery(id+"F41.opExtrude","SWEPT_BODY",BODY,{"disambiguationData":[OSD([sQuery(id+"F40.wireOp",EDGE,"E71.bottom"),sQuery(id+"F40.wireOp",EDGE,"E71.top"),sQuery(id+"F40.wireOp",EDGE,"E71.left"),sQuery(id+"F40.wireOp",EDGE,"E71.right")])]});
            var Q2;
            Q2=makeQuery(id+"F55.opExtrude","SWEPT_BODY",BODY,{"disambiguationData":[OSD([sQuery(id+"F54.wireOp",EDGE,"E78.bottom"),sQuery(id+"F54.wireOp",EDGE,"E78.top"),sQuery(id+"F54.wireOp",EDGE,"E78.left"),sQuery(id+"F54.wireOp",EDGE,"E78.right")])]});
            var Q3;
            Q3=makeQuery(id+"F69.opExtrude","SWEPT_BODY",BODY,{"disambiguationData":[OSD([sQuery(id+"F68.wireOp",EDGE,"E86.bottom"),sQuery(id+"F68.wireOp",EDGE,"E86.top"),sQuery(id+"F68.wireOp",EDGE,"E86.left"),sQuery(id+"F68.wireOp",EDGE,"E86.right")])]});
            var Q4;
            Q4=makeQuery(id+"F31.opPattern","COPY",BODY,{"derivedFrom":makeQuery(id+"F16.opExtrude","SWEPT_BODY",BODY,{"disambiguationData":[OSD([sQuery(id+"F15.wireOp",EDGE,"E50.bottom"),sQuery(id+"F15.wireOp",EDGE,"E50.top"),sQuery(id+"F15.wireOp",EDGE,"E50.left"),sQuery(id+"F15.wireOp",EDGE,"E50.right")])]}),"instanceName":"1"});
            var Q5;
            Q5=makeQuery(id+"F57.opExtrude","SWEPT_BODY",BODY,{"disambiguationData":[OSD([sQuery(id+"F56.wireOp",EDGE,"E79.bottom"),sQuery(id+"F56.wireOp",EDGE,"E79.top"),sQuery(id+"F56.wireOp",EDGE,"E79.left"),sQuery(id+"F56.wireOp",EDGE,"E79.right")])]});
            var Q6;
            Q6=makeQuery(id+"F47.opExtrude","SWEPT_BODY",BODY,{"disambiguationData":[OSD([sQuery(id+"F46.wireOp",EDGE,"E74.bottom"),sQuery(id+"F46.wireOp",EDGE,"E74.top"),sQuery(id+"F46.wireOp",EDGE,"E74.left"),sQuery(id+"F46.wireOp",EDGE,"E74.right")])]});
            var Q7;
            Q7=makeQuery(id+"F51.opExtrude","SWEPT_BODY",BODY,{"disambiguationData":[OSD([sQuery(id+"F50.wireOp",EDGE,"E76.bottom"),sQuery(id+"F50.wireOp",EDGE,"E76.top"),sQuery(id+"F50.wireOp",EDGE,"E76.left"),sQuery(id+"F50.wireOp",EDGE,"E76.right")])]});
            var Q8;
            Q8=makeQuery(id+"F63.opExtrude","SWEPT_BODY",BODY,{"disambiguationData":[OSD([sQuery(id+"F62.wireOp",EDGE,"E82.bottom"),sQuery(id+"F62.wireOp",EDGE,"E82.left"),sQuery(id+"F62.wireOp",EDGE,"E82.right"),sQuery(id+"F62.wireOp",EDGE,"E83.top"),sQuery(id+"F62.wireOp",EDGE,"E83.left"),sQuery(id+"F62.wireOp",EDGE,"E83.right")])]});
            var Q9;
            Q9=makeQuery(id+"F65.opExtrude","SWEPT_BODY",BODY,{"disambiguationData":[OSD([sQuery(id+"F64.wireOp",EDGE,"E84.bottom"),sQuery(id+"F64.wireOp",EDGE,"E84.top"),sQuery(id+"F64.wireOp",EDGE,"E84.left"),sQuery(id+"F64.wireOp",EDGE,"E84.right")])]});
            var Q10;
            Q10=makeQuery(id+"F59.opExtrude","SWEPT_BODY",BODY,{"disambiguationData":[OSD([sQuery(id+"F58.wireOp",EDGE,"E80.bottom"),sQuery(id+"F58.wireOp",EDGE,"E80.top"),sQuery(id+"F58.wireOp",EDGE,"E80.left"),sQuery(id+"F58.wireOp",EDGE,"E80.right")])]});
            var Q11;
            Q11=makeQuery(id+"F61.opExtrude","SWEPT_BODY",BODY,{"disambiguationData":[OSD([sQuery(id+"F60.wireOp",EDGE,"E81.bottom"),sQuery(id+"F60.wireOp",EDGE,"E81.top"),sQuery(id+"F60.wireOp",EDGE,"E81.left"),sQuery(id+"F60.wireOp",EDGE,"E81.right")])]});
            var Q12;
            Q12=makeQuery(id+"F45.opExtrude","SWEPT_BODY",BODY,{"disambiguationData":[OSD([sQuery(id+"F44.wireOp",EDGE,"E73.bottom"),sQuery(id+"F44.wireOp",EDGE,"E73.top"),sQuery(id+"F44.wireOp",EDGE,"E73.left"),sQuery(id+"F44.wireOp",EDGE,"E73.right")])]});
            var Q13;
            Q13=makeQuery(id+"F53.opExtrude","SWEPT_BODY",BODY,{"disambiguationData":[OSD([sQuery(id+"F52.wireOp",EDGE,"E77.bottom"),sQuery(id+"F52.wireOp",EDGE,"E77.top"),sQuery(id+"F52.wireOp",EDGE,"E77.left"),sQuery(id+"F52.wireOp",EDGE,"E77.right")])]});
            deleteBodies(context, id + "F72", {"entities" : qUnion([Q0, Q1, Q2, Q3, Q4, Q5, Q6, Q7, Q8, Q9, Q10, Q11, Q12, Q13])});
        }
        {
            var Q0;
            Q0=makeQuery(id+"F16.opExtrude","SWEPT_BODY",BODY,{"disambiguationData":[OSD([sQuery(id+"F15.wireOp",EDGE,"E50.bottom"),sQuery(id+"F15.wireOp",EDGE,"E50.top"),sQuery(id+"F15.wireOp",EDGE,"E50.left"),sQuery(id+"F15.wireOp",EDGE,"E50.right")])]});
            transform(context, id + "F73", {"entities" : qUnion([Q0]), "transformType" : TransformType.TRANSLATION_3D, "dx" : 44.6 * mm, "dy" : 0 * mm, "dz" : 60 * mm, "makeCopy" : true});
        }
        {
            var Q0;
            Q0=makeQuery(id+"F73.opPattern","COPY",FACE,{"derivedFrom":makeQuery(id+"F16.opExtrude","CAP_FACE",FACE,{"disambiguationData":[OSD([sQuery(id+"F15.wireOp",EDGE,"E50.bottom"),sQuery(id+"F15.wireOp",EDGE,"E50.top"),sQuery(id+"F15.wireOp",EDGE,"E50.left"),sQuery(id+"F15.wireOp",EDGE,"E50.right")])],"isStart":true}),"instanceName":"1"});
            var sketch = newSketch(context, id + "F74", { "sketchPlane" : qUnion([Q0])});
            skLineSegment(sketch, "E87.bottom", {"start": v(-33.25, 75.3) * mm, "end": v(0.5, 75.3) * mm});
            skLineSegment(sketch, "E87.top", {"start": v(-33.25, 62.5) * mm, "end": v(0.5, 62.5) * mm});
            skLineSegment(sketch, "E87.left", {"start": v(-33.25, 75.3) * mm, "end": v(-33.25, 62.5) * mm});
            skLineSegment(sketch, "E87.right", {"start": v(0.5, 75.3) * mm, "end": v(0.5, 62.5) * mm});
            skSolve(sketch);
        }
        {
            var Q0;
            Q0 = qSketchRegion(id + "F74", true);
            extrude(context, id + "F75", {"entities" : qUnion([Q0]), "depth" : 5 * mm, "offsetDistance" : 25 * mm});
        }
        {
            var Q0;
            Q0=makeQuery(id+"F75.opExtrude","SWEPT_FACE",FACE,{"disambiguationData":[OSD([sQuery(id+"F74.wireOp",EDGE,"E87.bottom")])]});
            var sketch = newSketch(context, id + "F76", { "sketchPlane" : qUnion([Q0])});
            skLineSegment(sketch, "E88.bottom", {"start": v(93.35, -0.5) * mm, "end": v(98.35, -0.5) * mm});
            skLineSegment(sketch, "E88.top", {"start": v(93.35, 33.25) * mm, "end": v(98.35, 33.25) * mm});
            skLineSegment(sketch, "E88.left", {"start": v(93.35, -0.5) * mm, "end": v(93.35, 33.25) * mm});
            skLineSegment(sketch, "E88.right", {"start": v(98.35, -0.5) * mm, "end": v(98.35, 33.25) * mm});
            skSolve(sketch);
        }
        {
            var Q0;
            Q0 = qSketchRegion(id + "F76", true);
            extrude(context, id + "F77", {"entities" : qUnion([Q0]), "operationType" : NewBodyOperationType.ADD, "depth" : 5 * mm, "offsetDistance" : 25 * mm});
        }
        {
            var Q0;
            Q0=makeQuery(id+"F77.boolean.opBoolean","MERGE",FACE,{"derivedFrom":[makeQuery(id+"F75.opExtrude","SWEPT_FACE",FACE,{"disambiguationData":[OSD([sQuery(id+"F74.wireOp",EDGE,"E87.left")])]}),makeQuery(id+"F77.opExtrude","SWEPT_FACE",FACE,{"disambiguationData":[OSD([sQuery(id+"F76.wireOp",EDGE,"E88.top")])]})]});
            var sketch = newSketch(context, id + "F78", { "sketchPlane" : qUnion([Q0])});
            skLineSegment(sketch, "E89.bottom", {"start": v(-93.35, 80.3) * mm, "end": v(-98.35, 80.3) * mm});
            skLineSegment(sketch, "E89.top", {"start": v(-93.35, 62.5) * mm, "end": v(-98.35, 62.5) * mm});
            skLineSegment(sketch, "E89.left", {"start": v(-93.35, 80.3) * mm, "end": v(-93.35, 62.5) * mm});
            skLineSegment(sketch, "E89.right", {"start": v(-98.35, 80.3) * mm, "end": v(-98.35, 62.5) * mm});
            skSolve(sketch);
        }
        {
            var Q0;
            Q0 = qSketchRegion(id + "F78", true);
            extrude(context, id + "F79", {"entities" : qUnion([Q0]), "operationType" : NewBodyOperationType.ADD, "depth" : 5 * mm, "offsetDistance" : 25 * mm});
        }
        {
            var Q0;
            Q0=makeQuery(id+"F77.boolean.opBoolean","MERGE",FACE,{"derivedFrom":[makeQuery(id+"F75.opExtrude","SWEPT_FACE",FACE,{"disambiguationData":[OSD([sQuery(id+"F74.wireOp",EDGE,"E87.right")])]}),makeQuery(id+"F77.opExtrude","SWEPT_FACE",FACE,{"disambiguationData":[OSD([sQuery(id+"F76.wireOp",EDGE,"E88.bottom")])]})]});
            var sketch = newSketch(context, id + "F80", { "sketchPlane" : qUnion([Q0])});
            skLineSegment(sketch, "E90.bottom", {"start": v(93.35, 80.3) * mm, "end": v(98.35, 80.3) * mm});
            skLineSegment(sketch, "E90.top", {"start": v(93.35, 62.5) * mm, "end": v(98.35, 62.5) * mm});
            skLineSegment(sketch, "E90.left", {"start": v(93.35, 80.3) * mm, "end": v(93.35, 62.5) * mm});
            skLineSegment(sketch, "E90.right", {"start": v(98.35, 80.3) * mm, "end": v(98.35, 62.5) * mm});
            skSolve(sketch);
        }
        {
            var Q0;
            Q0 = qSketchRegion(id + "F80", true);
            extrude(context, id + "F81", {"entities" : qUnion([Q0]), "operationType" : NewBodyOperationType.ADD, "depth" : 5 * mm, "offsetDistance" : 25 * mm});
        }
        {
            var Q0;
            Q0=makeQuery(id+"F81.boolean.opBoolean","MERGE",FACE,{"derivedFrom":[makeQuery(id+"F79.boolean.opBoolean","MERGE",FACE,{"derivedFrom":[makeQuery(id+"F75.opExtrude","SWEPT_FACE",FACE,{"disambiguationData":[OSD([sQuery(id+"F74.wireOp",EDGE,"E87.top")])]}),makeQuery(id+"F79.opExtrude","SWEPT_FACE",FACE,{"disambiguationData":[OSD([sQuery(id+"F78.wireOp",EDGE,"E89.top")])]})]}),makeQuery(id+"F81.opExtrude","SWEPT_FACE",FACE,{"disambiguationData":[OSD([sQuery(id+"F80.wireOp",EDGE,"E90.top")])]})]});
            var sketch = newSketch(context, id + "F82", { "sketchPlane" : qUnion([Q0])});
            skLineSegment(sketch, "E91.bottom", {"start": v(93.35, -38.25) * mm, "end": v(98.35, -38.25) * mm});
            skLineSegment(sketch, "E91.top", {"start": v(93.35, 5.5) * mm, "end": v(98.35, 5.5) * mm});
            skLineSegment(sketch, "E91.left", {"start": v(93.35, -38.25) * mm, "end": v(93.35, 5.5) * mm});
            skLineSegment(sketch, "E91.right", {"start": v(98.35, -38.25) * mm, "end": v(98.35, 5.5) * mm});
            skSolve(sketch);
        }
        {
            var Q0;
            Q0 = qSketchRegion(id + "F82", true);
            extrude(context, id + "F83", {"entities" : qUnion([Q0]), "operationType" : NewBodyOperationType.ADD, "depth" : 5 * mm, "offsetDistance" : 25 * mm});
        }
    });
